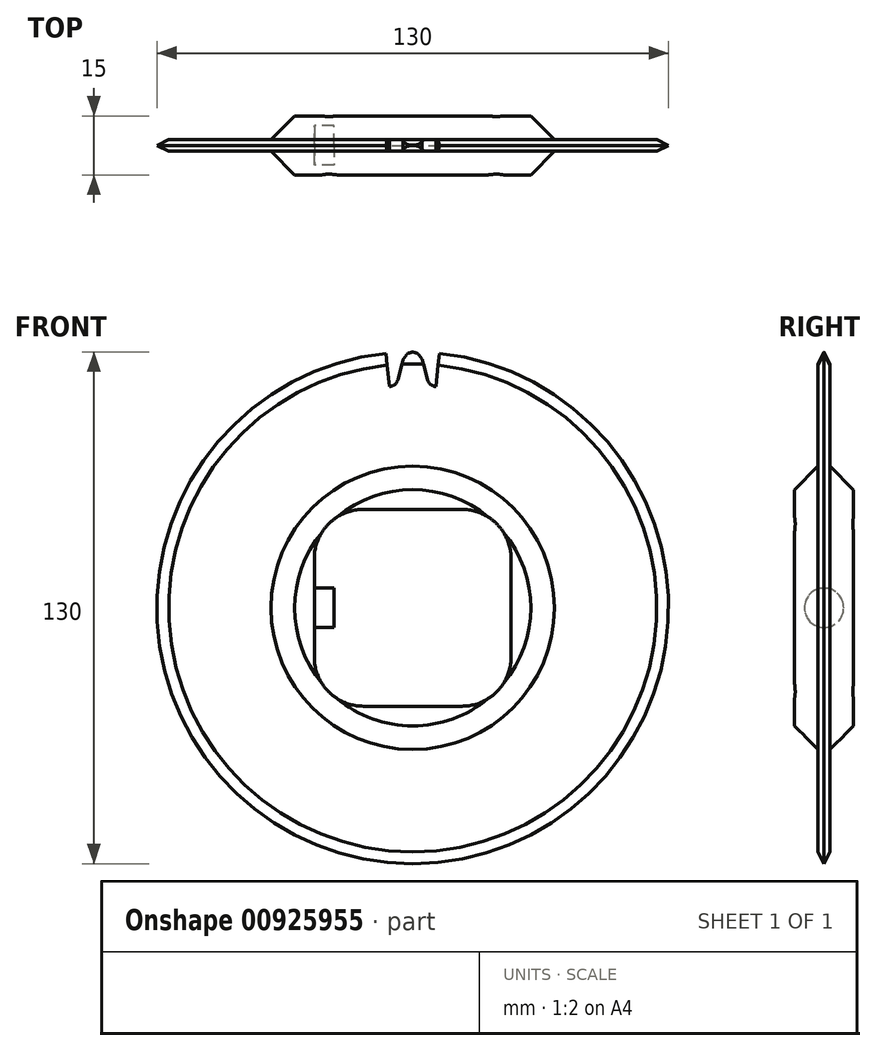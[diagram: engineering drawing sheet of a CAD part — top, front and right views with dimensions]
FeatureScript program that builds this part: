
annotation { "Feature Type Name" : "Feature", "Feature Type Description" : "" }
export const myFeature = defineFeature(function(context is Context, id is Id, definition is map)
    precondition{}
    {
        {
            var Q0;
            Q0=qCreatedBy(makeId("Right.planeOp"),FACE);
            var sketch = newSketch(context, id + "F0", { "sketchPlane" : qUnion([Q0])});
            skLineSegment(sketch, "E0", {"start": v(0, 0) * mm, "end": v(7.5, 0) * mm});
            skLineSegment(sketch, "E1", {"start": v(7.5, 0) * mm, "end": v(7.5, 30) * mm});
            skLineSegment(sketch, "E2", {"start": v(7.5, 30) * mm, "end": v(1.5, 36) * mm});
            skLineSegment(sketch, "E3", {"start": v(1.5, 36) * mm, "end": v(1.5, 62) * mm});
            skLineSegment(sketch, "E4", {"start": v(1.5, 62) * mm, "end": v(0, 65) * mm});
            skLineSegment(sketch, "E5", {"start": v(0, 65) * mm, "end": v(0, 0) * mm});
            skSolve(sketch);
        }
        {
            var Q0;
            Q0=makeQuery(id+"F0.imprint","IMPRINT",FACE,{"disambiguationData":[TD([[makeQuery(id+"F0.imprint","IMPRINT",EDGE,{"derivedFrom":sQuery(id+"F0.wireOp",EDGE,"E0")}),1.0]])]});
            var Q1;
            Q1=sQuery(id+"F0.wireOp",EDGE,"E0");
            revolve(context, id + "F1", {"surfaceOperationType" : NewSurfaceOperationType.NEW, "entities" : qUnion([Q0]), "axis" : qUnion([Q1]), "revolveType" : RevolveType.FULL});
        }
        {
            var Q0;
            Q0=makeQuery(id+"F1.opRevolve","SWEPT_FACE",FACE,{"disambiguationData":[OSD([sQuery(id+"F0.wireOp",EDGE,"E5")])]});
            var sketch = newSketch(context, id + "F2", { "sketchPlane" : qUnion([Q0])});
            skLineSegment(sketch, "E6", {"start": v(0, 0) * mm, "end": v(-6.8, 64.64) * mm, "construction": true});
            skLineSegment(sketch, "E7", {"start": v(-6.8, 64.64) * mm, "end": v(6.8, 64.64) * mm, "construction": true});
            skLineSegment(sketch, "E8", {"start": v(6.8, 64.64) * mm, "end": v(0, 0) * mm, "construction": true});
            skCircle(sketch, "E9", {"center": v(0, 0) * mm, "radius": 62.5 * mm, "construction": true});
            skCircle(sketch, "E10", {"center": v(0, 0) * mm, "radius": 59 * mm, "construction": true});
            skCircle(sketch, "E11", {"center": v(0, 62.5) * mm, "radius": 2.5 * mm, "construction": true});
            skArc(sketch, "E12", {"start": v(-5.9, 56.2) * mm, "mid": v(-4.54, 56.78) * mm, "end": v(-3.75, 58.04) * mm});
            skArc(sketch, "E13", {"start": v(3.75, 58.04) * mm, "mid": v(4.54, 56.78) * mm, "end": v(5.9, 56.2) * mm});
            skLineSegment(sketch, "E14", {"start": v(-2.42, 63.13) * mm, "end": v(-3.75, 58.04) * mm});
            skLineSegment(sketch, "E15", {"start": v(3.75, 58.04) * mm, "end": v(2.42, 63.13) * mm});
            skLineSegment(sketch, "E16", {"start": v(-2.42, 63.13) * mm, "end": v(-1.29, 64.64) * mm});
            skLineSegment(sketch, "E17", {"start": v(-1.29, 64.64) * mm, "end": v(0, 65.01) * mm});
            skPoint(sketch, "E17.endSnap0", {"position": v(0, 64.64) * mm});
            skLineSegment(sketch, "E18", {"start": v(0, 65.01) * mm, "end": v(1.29, 64.64) * mm});
            skLineSegment(sketch, "E19", {"start": v(-5.9, 56.2) * mm, "end": v(-6.8, 64.64) * mm});
            skLineSegment(sketch, "E20", {"start": v(-6.8, 64.64) * mm, "end": v(0, 70.01) * mm});
            skLineSegment(sketch, "E21", {"start": v(0, 70.01) * mm, "end": v(6.8, 64.64) * mm});
            skLineSegment(sketch, "E22", {"start": v(1.29, 64.64) * mm, "end": v(2.42, 63.13) * mm});
            skLineSegment(sketch, "E23", {"start": v(6.8, 64.64) * mm, "end": v(5.9, 56.2) * mm});
            skSolve(sketch);
        }
        {
            var Q0;
            Q0 = qSketchRegion(id + "FivPJYXdHNzPAt2_1", true);
            var Q1;
            Q1 = qSketchRegion(id + "F2", true);
            extrude(context, id + "F3", {"entities" : qUnion([Q0, Q1]), "operationType" : NewBodyOperationType.REMOVE, "endBound" : BoundingType.THROUGH_ALL, "oppositeDirection" : true, "depth" : 25 * mm, "offsetDistance" : 25 * mm});
        }
        {
            var Q0;
            Q0=qCreatedBy(makeId("Front.planeOp"),FACE);
            var sketch = newSketch(context, id + "F4", { "sketchPlane" : qUnion([Q0])});
            skCircle(sketch, "E24", {"center": v(0, 0) * mm, "radius": 25 * mm, "construction": true});
            skLineSegment(sketch, "E25.bottom", {"start": v(12.5, 25) * mm, "end": v(-12.5, 25) * mm});
            skLineSegment(sketch, "E25.top", {"start": v(12.5, -25) * mm, "end": v(-12.5, -25) * mm});
            skLineSegment(sketch, "E25.left", {"start": v(25, 12.5) * mm, "end": v(25, -12.5) * mm});
            skLineSegment(sketch, "E25.right", {"start": v(-25, 12.5) * mm, "end": v(-25, -12.5) * mm});
            skPoint(sketch, "E26.visualSharp", {"position": v(25, -25) * mm});
            skArc(sketch, "E26.filletArc", {"start": v(12.5, -25) * mm, "mid": v(21.34, -21.34) * mm, "end": v(25, -12.5) * mm});
            skPoint(sketch, "E27.visualSharp", {"position": v(-25, -25) * mm});
            skArc(sketch, "E27.filletArc", {"start": v(-25, -12.5) * mm, "mid": v(-21.34, -21.34) * mm, "end": v(-12.5, -25) * mm});
            skPoint(sketch, "E28.visualSharp", {"position": v(-25, 25) * mm});
            skArc(sketch, "E28.filletArc", {"start": v(-12.5, 25) * mm, "mid": v(-21.34, 21.34) * mm, "end": v(-25, 12.5) * mm});
            skPoint(sketch, "E29.visualSharp", {"position": v(25, 25) * mm});
            skArc(sketch, "E29.filletArc", {"start": v(25, 12.5) * mm, "mid": v(21.34, 21.34) * mm, "end": v(12.5, 25) * mm});
            skSolve(sketch);
        }
        {
            var Q0;
            Q0 = qSketchRegion(id + "F4", true);
            extrude(context, id + "F5", {"entities" : qUnion([Q0]), "operationType" : NewBodyOperationType.REMOVE, "endBound" : BoundingType.THROUGH_ALL, "oppositeDirection" : true, "depth" : 25 * mm, "offsetDistance" : 25 * mm});
        }
        {
            var Q0;
            Q0=makeQuery(id+"F1.opRevolve","SWEPT_BODY",BODY,{"disambiguationData":[OSD([sQuery(id+"F0.wireOp",EDGE,"E0"),sQuery(id+"F0.wireOp",EDGE,"E1"),sQuery(id+"F0.wireOp",EDGE,"E2"),sQuery(id+"F0.wireOp",EDGE,"E3"),sQuery(id+"F0.wireOp",EDGE,"E4"),sQuery(id+"F0.wireOp",EDGE,"E5")])]});
            var Q1;
            Q1=qCreatedBy(makeId("Front.planeOp"),FACE);
            mirror(context, id + "F6", {"operationType" : NewBodyOperationType.ADD, "entities" : qUnion([Q0]), "mirrorPlane" : qUnion([Q1])});
        }
        {
            var Q0;
            {var subQ0=makeQuery(id+"F5.boolean.opBoolean","COPY",FACE,{"derivedFrom":makeQuery(id+"F5.opExtrude","SWEPT_FACE",FACE,{"disambiguationData":[OSD([sQuery(id+"F4.wireOp",EDGE,"E25.right")])]})});Q0=makeQuery(id+"F6.boolean.opBoolean","MERGE",FACE,{"derivedFrom":[subQ0,makeQuery(id+"F6.opPattern","COPY",FACE,{"derivedFrom":subQ0,"instanceName":"1"})]});}
            var sketch = newSketch(context, id + "F7", { "sketchPlane" : qUnion([Q0])});
            skCircle(sketch, "E30", {"center": v(0, 0) * mm, "radius": 5 * mm});
            skSolve(sketch);
        }
        {
            var Q0;
            Q0 = qSketchRegion(id + "F7", true);
            extrude(context, id + "F8", {"entities" : qUnion([Q0]), "operationType" : NewBodyOperationType.ADD, "depth" : 5 * mm, "offsetDistance" : 25 * mm});
        }
    });
